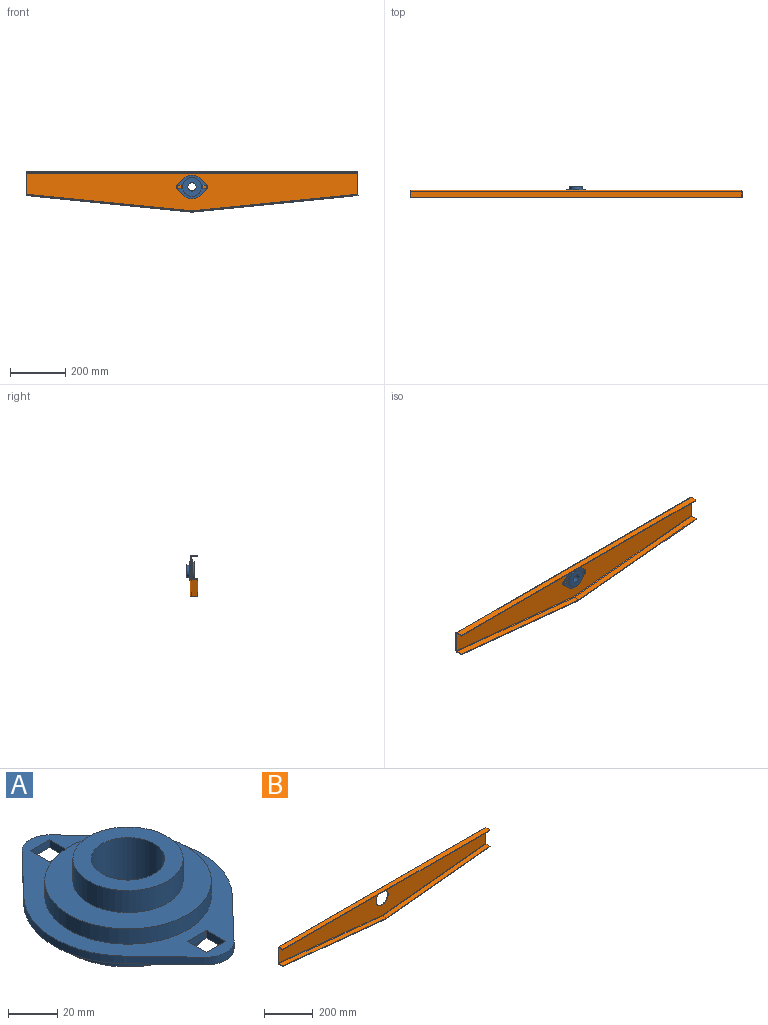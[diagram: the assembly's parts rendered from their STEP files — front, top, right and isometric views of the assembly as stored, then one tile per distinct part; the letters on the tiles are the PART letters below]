
ASSEMBLY  parts=2 mates=1
PART A: 25 faces, bbox 85x113x30 mm
  f0: plane 113x85mm, normal (0,0,-1), area 2602.9mm2, adj f1,f2,f4,f5,f6,f7,f8,f9
  f1: plane 11x3.8mm, normal (-1,0,0), area 41.8mm2, adj f0,f2,f3,f13
  f2: plane 11x3.8mm, normal (0,1,0), area 41.8mm2, adj f0,f1,f3,f24
  f3: plane 113x85mm, normal (0,0,1), area 2602.9mm2, adj f1,f2,f4,f5,f6,f7,f8,f9
  f4: plane 23.67x22.6mm, normal (-0.72,0.69,0), area 124.4mm2, adj f0,f3,f5,f11
  f5: cylinder r=11.25mm len=16.27mm, axis (0,0,1), area 69.1mm2, adj f0,f3,f4,f6
  f6: plane 23.67x22.6mm, normal (0.72,0.69,0), area 124.4mm2, adj f0,f3,f5,f7
  f7: cylinder r=42.5mm len=58.7mm, axis (0,0,1), area 246.2mm2, adj f0,f3,f6,f8
  f8: plane 23.67x22.6mm, normal (0.72,-0.69,0), area 124.4mm2, adj f0,f3,f7,f9
  f9: cylinder r=11.25mm len=16.27mm, axis (0,0,1), area 69.1mm2, adj f0,f3,f8,f10
  f10: plane 23.67x22.6mm, normal (-0.72,-0.69,0), area 124.4mm2, adj f0,f3,f9,f11
  f11: cylinder r=42.5mm len=58.7mm, axis (0,0,1), area 246.2mm2, adj f0,f3,f4,f10
  f12: plane 11x3.8mm, normal (-1,0,0), area 41.8mm2, adj f0,f3,f14,f16
  f13: plane 11x3.8mm, normal (0,-1,0), area 41.8mm2, adj f0,f1,f3,f24
  f14: plane 11x3.8mm, normal (0,1,0), area 41.8mm2, adj f0,f3,f12,f15
  f15: plane 11x3.8mm, normal (1,0,0), area 41.8mm2, adj f0,f3,f14,f16
  f16: plane 11x3.8mm, normal (0,-1,0), area 41.8mm2, adj f0,f3,f12,f15
  f17: cylinder r=15mm len=30mm, axis (0,0,1), area 2827.4mm2, adj f18,f21
  f18: plane 45x45mm, normal (0,0,1), area 883.6mm2, adj f17,f19
  f19: cylinder r=22.5mm len=45mm, axis (0,0,1), area 1555.1mm2, adj f18,f20
  f20: plane 68x68mm, normal (0,0,1), area 2041.2mm2, adj f19,f23
  f21: plane 68x68mm, normal (0,0,-1), area 2924.8mm2, adj f17,f22
  f22: cylinder r=34mm len=68mm, axis (0,0,1), area 1623.6mm2, adj f0,f21
  f23: cylinder r=34mm len=68mm, axis (0,0,1), area 1623.6mm2, adj f3,f20
  f24: plane 11x3.8mm, normal (1,0,0), area 41.8mm2, adj f0,f2,f3,f13
PART B: 35 faces, bbox 1201x28x146 mm
  f0: plane 75.99x3mm, normal (-1,0,0), area 228mm2, adj f3,f4,f21,f32
  f1: plane 75.99x3mm, normal (1,0,0), area 228mm2, adj f3,f4,f11,f31
  f2: cylinder r=35mm len=70mm, axis (0,-1,0), area 659.7mm2, adj f3,f4
  f3: plane 1200x135.99mm, normal (0,1,0), area 123339.6mm2, adj f0,f1,f2,f13,f23,f33
  f4: plane 1200x135.99mm, normal (0,-1,0), area 123339.6mm2, adj f0,f1,f2,f14,f24,f34
  f5: plane 3x0.49mm, normal (0,1,0), area 0.6mm2, adj f7,f9,f10,f12
  f6: plane 600.29x62.98mm, normal (0,-1,0), area 1808.9mm2, adj f7,f8,f9,f10
  f7: plane 23x2.99mm, normal (-1,0,-0.1), area 69mm2, adj f5,f6,f9,f10
  f8: plane 23x2.99mm, normal (1,0,0.1), area 69mm2, adj f6,f9,f10,f11
  f9: plane 599.99x60mm, normal (0.1,0,-1), area 13868.6mm2, adj f5,f6,f7,f8,f13
  f10: plane 599.99x60mm, normal (-0.1,0,1), area 13868.6mm2, adj f5,f6,f7,f8,f14
  f11: bspline ~5x5mm, area 16.5mm2, adj f1,f8,f13,f14
  f12: plane 5x4.98mm, normal (-1,0,-0.1), area 16.5mm2, adj f5,f13,f14,f22
  f13: cylinder r=5mm len=600.5mm, axis (1,0,0.1), area 4735.1mm2, adj f3,f9,f11,f12
  f14: cylinder r=2mm len=600.2mm, axis (1,0,0.1), area 1894mm2, adj f4,f10,f11,f12
  f15: plane 600.29x62.98mm, normal (0,-1,0), area 1808.9mm2, adj f16,f18,f19,f20
  f16: plane 23x2.99mm, normal (-1,0,0.1), area 69mm2, adj f15,f19,f20,f21
  f17: plane 3x0.49mm, normal (0,1,0), area 0.6mm2, adj f18,f19,f20,f22
  f18: plane 23x2.99mm, normal (1,0,-0.1), area 69mm2, adj f15,f17,f19,f20
  f19: plane 599.99x60mm, normal (-0.1,0,-1), area 13868.6mm2, adj f15,f16,f17,f18,f23
  f20: plane 599.99x60mm, normal (0.1,0,1), area 13868.6mm2, adj f15,f16,f17,f18,f24
  f21: bspline ~5x5mm, area 16.5mm2, adj f0,f16,f23,f24
  f22: plane 5x4.98mm, normal (1,0,-0.1), area 16.5mm2, adj f12,f17,f23,f24
  f23: cylinder r=5mm len=600.5mm, axis (-1,0,0.1), area 4735.1mm2, adj f3,f19,f21,f22
  f24: cylinder r=2mm len=600.2mm, axis (-1,0,0.1), area 1894mm2, adj f4,f20,f21,f22
  f25: plane 1195x3mm, normal (0,-1,0), area 3585mm2, adj f27,f28,f29,f30
  f26: plane 18x3mm, normal (1,0,0), area 54mm2, adj f28,f29,f30,f31
  f27: plane 23x3mm, normal (-1,0,0), area 69mm2, adj f25,f28,f29,f32
  f28: plane 1200x23mm, normal (0,0,1), area 27594.6mm2, adj f25,f26,f27,f30,f33
  f29: plane 1200x23mm, normal (0,0,-1), area 27594.6mm2, adj f25,f26,f27,f30,f34
  f30: cylinder r=5mm len=5mm, axis (0,0,1), area 23.6mm2, adj f25,f26,f28,f29
  f31: plane 5x5mm, normal (1,0,0), area 16.5mm2, adj f1,f26,f33,f34
  f32: plane 5x5mm, normal (-1,0,0), area 16.5mm2, adj f0,f27,f33,f34
  f33: cylinder r=5mm len=1200mm, axis (1,0,0), area 9424.8mm2, adj f3,f28,f31,f32
  f34: cylinder r=2mm len=1200mm, axis (1,0,0), area 3769.9mm2, adj f4,f29,f31,f32
PLACE A rot(axis=(-0.58,0.58,0.58),120deg) t=(-738.45,40.56,203.63)mm
PLACE B t=(-738.45,43.06,215.16)mm
MATE fastened A.f17 <-> B.f2  axis (0,-1,0) through (-738.45,31.06,203.63)mm
